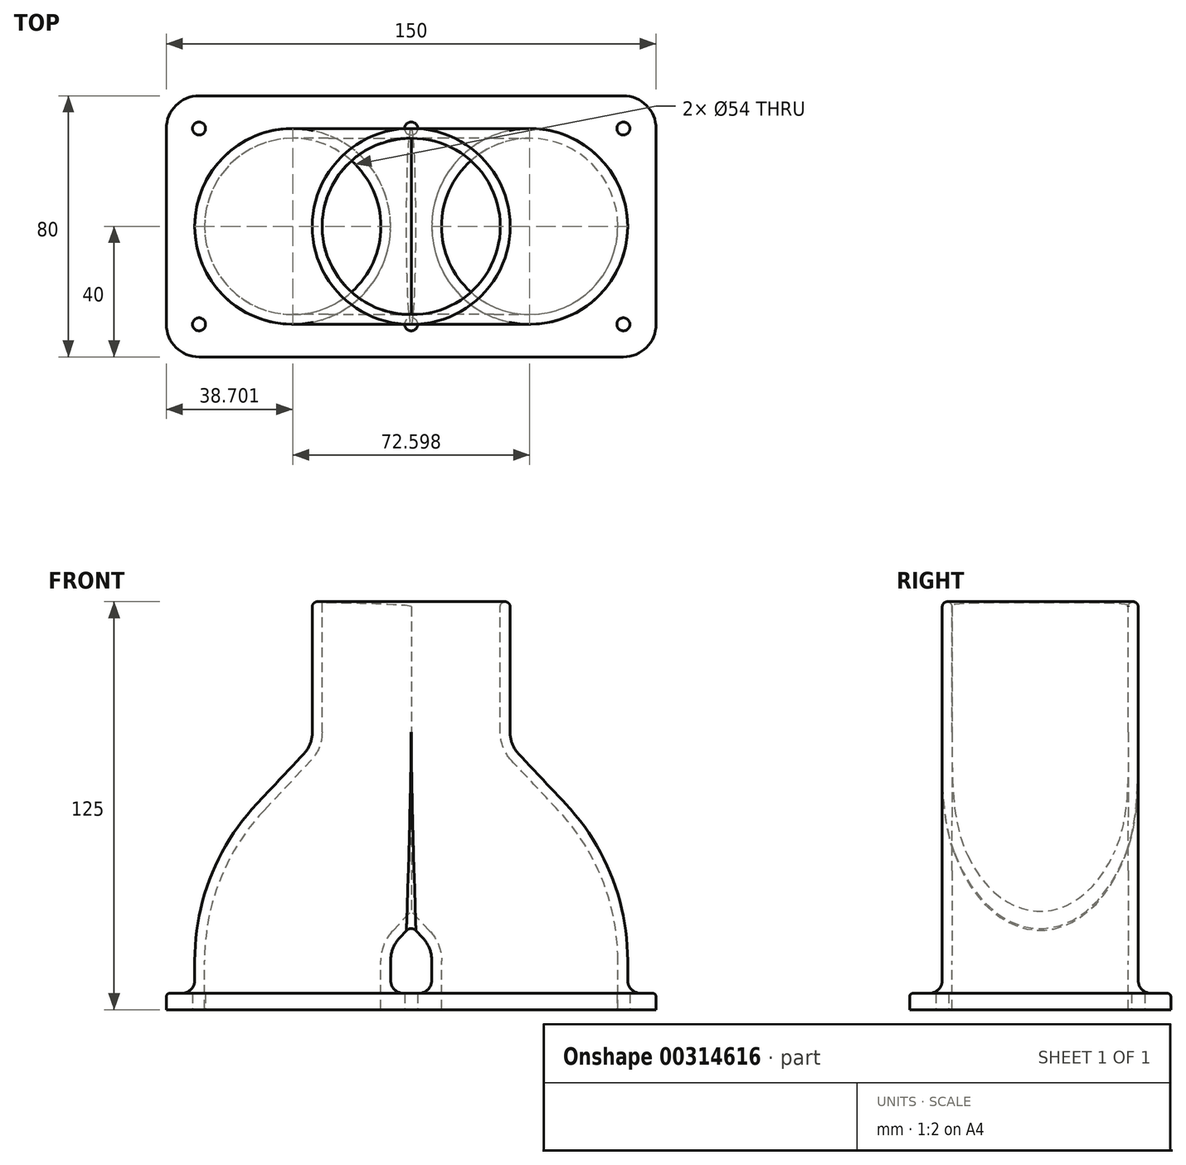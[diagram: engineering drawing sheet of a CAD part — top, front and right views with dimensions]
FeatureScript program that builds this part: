
annotation { "Feature Type Name" : "Feature", "Feature Type Description" : "" }
export const myFeature = defineFeature(function(context is Context, id is Id, definition is map)
    precondition{}
    {
        {
            var Q0;
            Q0=qCreatedBy(makeId("Front.planeOp"),FACE);
            var sketch = newSketch(context, id + "F0", { "sketchPlane" : qUnion([Q0])});
            skLineSegment(sketch, "E0", {"start": v(36, 0) * mm, "end": v(36, 15) * mm});
            skLineSegment(sketch, "E1", {"start": v(0, 125) * mm, "end": v(80.75, 125) * mm, "construction": true});
            skLineSegment(sketch, "E2", {"start": v(0, 85) * mm, "end": v(81.82, 85) * mm, "construction": true});
            skLineSegment(sketch, "E3", {"start": v(40, 109.76) * mm, "end": v(40, 63.63) * mm, "construction": true});
            skLineSegment(sketch, "E4", {"start": v(-4, 0) * mm, "end": v(-4, 33.23) * mm, "construction": true});
            skLineSegment(sketch, "E5", {"start": v(36, 15) * mm, "end": v(-30.05, 15) * mm, "construction": true});
            skArc(sketch, "E6", {"start": v(36, 15) * mm, "mid": v(33.19, 29.73) * mm, "end": v(25.15, 42.4) * mm});
            skArc(sketch, "E7", {"start": v(0, 85) * mm, "mid": v(2.81, 70.27) * mm, "end": v(10.85, 57.6) * mm});
            skLineSegment(sketch, "E8", {"start": v(25.15, 42.4) * mm, "end": v(10.85, 57.6) * mm});
            skLineSegment(sketch, "E9.trimOffspring", {"start": v(0, 85) * mm, "end": v(0, 125) * mm});
            skLineSegment(sketch, "E10", {"start": v(0, 0) * mm, "end": v(0, 134.4) * mm, "construction": true});
            skSolve(sketch);
        }
        {
            var Q0;
            Q0=qCreatedBy(makeId("Top.planeOp"),FACE);
            var sketch = newSketch(context, id + "F1", { "sketchPlane" : qUnion([Q0])});
            skCircle(sketch, "E11", {"center": v(36.3, 0) * mm, "radius": 30 * mm});
            skSolve(sketch);
        }
        {
            var Q0;
            Q0=makeQuery(id+"F1.imprint","IMPRINT",FACE,{"disambiguationData":[TD([[makeQuery(id+"F1.imprint","IMPRINT",EDGE,{"derivedFrom":sQuery(id+"F1.wireOp",EDGE,"E11")}),1.0]])]});
            var Q1;
            Q1=sQuery(id+"F0.wireOp",EDGE,"E0");
            var Q2;
            Q2=sQuery(id+"F0.wireOp",EDGE,"E6");
            var Q3;
            Q3=sQuery(id+"F0.wireOp",EDGE,"E8");
            var Q4;
            Q4=sQuery(id+"F0.wireOp",EDGE,"E7");
            var Q5;
            Q5=sQuery(id+"F0.wireOp",EDGE,"E9.trimOffspring");
            sweep(context, id + "F2", {"profiles" : qUnion([Q0]), "path" : qUnion([Q1, Q2, Q3, Q4, Q5])});
        }
        {
            var Q0;
            Q0=makeQuery(id+"F2.opSweep","SWEPT_BODY",BODY,{"disambiguationData":[OSD([sQuery(id+"F0.wireOp",EDGE,"E9.trimOffspring"),sQuery(id+"F1.wireOp",EDGE,"E11")])]});
            var Q1;
            Q1=qCreatedBy(makeId("Right.planeOp"),FACE);
            mirror(context, id + "F3", {"entities" : qUnion([Q0]), "mirrorPlane" : qUnion([Q1])});
        }
        {
            var Q0;
            Q0=makeQuery(id+"F3.opPattern","COPY",BODY,{"derivedFrom":makeQuery(id+"F2.opSweep","SWEPT_BODY",BODY,{"disambiguationData":[OSD([sQuery(id+"F0.wireOp",EDGE,"E9.trimOffspring"),sQuery(id+"F1.wireOp",EDGE,"E11")])]}),"instanceName":"1"});
            var Q1;
            Q1=makeQuery(id+"F2.opSweep","SWEPT_BODY",BODY,{"disambiguationData":[OSD([sQuery(id+"F0.wireOp",EDGE,"E9.trimOffspring"),sQuery(id+"F1.wireOp",EDGE,"E11")])]});
            booleanBodies(context, id + "F4", {"operationType" : BooleanOperationType.UNION, "tools" : qUnion([Q0, Q1])});
        }
        {
            var Q0;
            {var subQ0=makeQuery(id+"F2.opSweep","CAP_FACE",FACE,{"disambiguationData":[OSD([sQuery(id+"F0.wireOp",VERTEX,"E9.trimOffspring.end"),sQuery(id+"F1.wireOp",EDGE,"E11")])],"isStart":false});Q0=makeQuery(id+"F4.opBoolean","MERGE",FACE,{"derivedFrom":[subQ0,makeQuery(id+"F3.opPattern","COPY",FACE,{"derivedFrom":subQ0,"instanceName":"1"})]});}
            var Q1;
            Q1=makeQuery(id+"F2.opSweep","CAP_FACE",FACE,{"disambiguationData":[OSD([sQuery(id+"F0.wireOp",VERTEX,"E0.start"),sQuery(id+"F1.wireOp",EDGE,"E11")])],"isStart":true});
            var Q2;
            Q2=makeQuery(id+"F3.opPattern","COPY",FACE,{"derivedFrom":makeQuery(id+"F2.opSweep","CAP_FACE",FACE,{"disambiguationData":[OSD([sQuery(id+"F0.wireOp",VERTEX,"E0.start"),sQuery(id+"F1.wireOp",EDGE,"E11")])],"isStart":true}),"instanceName":"1"});
            shell(context, id + "F5", {"entities" : qUnion([Q0, Q1, Q2]), "thickness" : 3 * mm});
        }
        {
            var Q0;
            {var subQ0=makeQuery(id+"F2.opSweep","SWEPT_FACE",FACE,{"disambiguationData":[OSD([sQuery(id+"F0.wireOp",EDGE,"E8"),sQuery(id+"F1.wireOp",EDGE,"E11")])]});Q0=makeQuery(id+"F4.opBoolean","INTERSECT",EDGE,{"derivedFrom":[subQ0,makeQuery(id+"F3.opPattern","COPY",FACE,{"derivedFrom":subQ0,"instanceName":"1"})]});}
            fillet(context, id + "F6", {"entities" : qUnion([Q0]), "radius" : 2 * mm, "tangentPropagation" : true, "allowEdgeOverflow" : false});
        }
        {
            var Q0;
            Q0=qCreatedBy(makeId("Top.planeOp"),FACE);
            var sketch = newSketch(context, id + "F7", { "sketchPlane" : qUnion([Q0])});
            skLineSegment(sketch, "E12.bottom", {"start": v(-75, 40) * mm, "end": v(75, 40) * mm});
            skLineSegment(sketch, "E12.top", {"start": v(-75, -40) * mm, "end": v(75, -40) * mm});
            skLineSegment(sketch, "E12.left", {"start": v(-75, 40) * mm, "end": v(-75, -40) * mm});
            skLineSegment(sketch, "E12.right", {"start": v(75, 40) * mm, "end": v(75, -40) * mm});
            skPoint(sketch, "E13", {"position": v(-7.12, -183.95) * mm});
            skPoint(sketch, "E14", {"position": v(-65, -30) * mm});
            skPoint(sketch, "E15", {"position": v(65, -30) * mm});
            skPoint(sketch, "E16", {"position": v(65, 30) * mm});
            skPoint(sketch, "E17", {"position": v(-65, 30) * mm});
            skPoint(sketch, "E18", {"position": v(0, -30) * mm});
            skPoint(sketch, "E19", {"position": v(0, 30) * mm});
            skSolve(sketch);
        }
        {
            var Q0;
            Q0=makeQuery(id+"F7.imprint","IMPRINT",FACE,{"disambiguationData":[TD([[makeQuery(id+"F7.imprint","IMPRINT",EDGE,{"derivedFrom":sQuery(id+"F7.wireOp",EDGE,"E12.bottom")}),-1.0]])]});
            extrude(context, id + "F8", {"entities" : qUnion([Q0]), "operationType" : NewBodyOperationType.ADD, "depth" : 5 * mm});
        }
        {
            var Q0;
            {var subQ0=sQuery(id+"F1.wireOp",EDGE,"E11");var subQ1=sQuery(id+"F0.wireOp",EDGE,"E0");Q0=makeQuery(id+"F8.boolean.opBoolean","SPLIT",FACE,{"disambiguationData":[TD([makeQuery(id+"F5.opShell","OFFSET_FACE",FACE,{"disambiguationData":[OSD([subQ1,subQ0]),TDD([makeQuery(id+"F2.opSweep","SWEPT_FACE",FACE,{"disambiguationData":[OSD([subQ1,subQ0])]})])]})])],"derivedFrom":makeQuery(id+"F8.opExtrude","CAP_FACE",FACE,{"disambiguationData":[OSD([sQuery(id+"F7.wireOp",EDGE,"E12.bottom"),sQuery(id+"F7.wireOp",EDGE,"E12.top"),sQuery(id+"F7.wireOp",EDGE,"E12.left"),sQuery(id+"F7.wireOp",EDGE,"E12.right")])],"isStart":false})});}
            extrude(context, id + "F9", {"entities" : qUnion([Q0]), "operationType" : NewBodyOperationType.REMOVE, "oppositeDirection" : true, "depth" : 5 * mm});
        }
        {
            var Q0;
            {var subQ0=sQuery(id+"F1.wireOp",EDGE,"E11");var subQ1=sQuery(id+"F0.wireOp",EDGE,"E0");Q0=makeQuery(id+"F8.boolean.opBoolean","SPLIT",FACE,{"disambiguationData":[TD([makeQuery(id+"F5.opShell","OFFSET_FACE",FACE,{"disambiguationData":[OSD([subQ1,subQ0]),TDD([makeQuery(id+"F3.opPattern","COPY",FACE,{"derivedFrom":makeQuery(id+"F2.opSweep","SWEPT_FACE",FACE,{"disambiguationData":[OSD([subQ1,subQ0])]}),"instanceName":"1"})])]})])],"derivedFrom":makeQuery(id+"F8.opExtrude","CAP_FACE",FACE,{"disambiguationData":[OSD([sQuery(id+"F7.wireOp",EDGE,"E12.bottom"),sQuery(id+"F7.wireOp",EDGE,"E12.top"),sQuery(id+"F7.wireOp",EDGE,"E12.left"),sQuery(id+"F7.wireOp",EDGE,"E12.right")])],"isStart":false})});}
            extrude(context, id + "F10", {"entities" : qUnion([Q0]), "operationType" : NewBodyOperationType.REMOVE, "oppositeDirection" : true, "depth" : 5 * mm});
        }
        {
            var Q0;
            Q0=sQuery(id+"F7.wireOp",VERTEX,"E14");
            var Q1;
            Q1=sQuery(id+"F7.wireOp",VERTEX,"E15");
            var Q2;
            Q2=sQuery(id+"F7.wireOp",VERTEX,"E16");
            var Q3;
            Q3=sQuery(id+"F7.wireOp",VERTEX,"E17");
            var Q4;
            Q4=sQuery(id+"F7.wireOp",VERTEX,"E18");
            var Q5;
            Q5=sQuery(id+"F7.wireOp",VERTEX,"E19");
            var Q6;
            Q6=makeQuery(id+"F3.opPattern","COPY",BODY,{"derivedFrom":makeQuery(id+"F2.opSweep","SWEPT_BODY",BODY,{"disambiguationData":[OSD([sQuery(id+"F0.wireOp",EDGE,"E9.trimOffspring"),sQuery(id+"F1.wireOp",EDGE,"E11")])]}),"instanceName":"1"});
            hole(context, id + "F11", {"style" : HoleStyle.SIMPLE, "endStyle" : HoleEndStyle.BLIND, "oppositeDirection" : true, "holeDiameter" : 4 * mm, "holeDepth" : 5 * mm, "tappedDepth" : 12 * mm, "tapClearance" : 3, "startFromSketch" : true, "locations" : qUnion([Q0, Q1, Q2, Q3, Q4, Q5]), "scope" : qUnion([Q6])});
        }
        {
            var Q0;
            Q0=makeQuery(id+"F8.opExtrude","SWEPT_EDGE",EDGE,{"disambiguationData":[OSD([sQuery(id+"F7.wireOp",EDGE,"E12.top"),sQuery(id+"F7.wireOp",EDGE,"E12.right")])]});
            var Q1;
            Q1=makeQuery(id+"F8.opExtrude","SWEPT_EDGE",EDGE,{"disambiguationData":[OSD([sQuery(id+"F7.wireOp",EDGE,"E12.top"),sQuery(id+"F7.wireOp",EDGE,"E12.left")])]});
            var Q2;
            Q2=makeQuery(id+"F8.opExtrude","SWEPT_EDGE",EDGE,{"disambiguationData":[OSD([sQuery(id+"F7.wireOp",EDGE,"E12.bottom"),sQuery(id+"F7.wireOp",EDGE,"E12.right")])]});
            var Q3;
            Q3=makeQuery(id+"F8.opExtrude","SWEPT_EDGE",EDGE,{"disambiguationData":[OSD([sQuery(id+"F7.wireOp",EDGE,"E12.bottom"),sQuery(id+"F7.wireOp",EDGE,"E12.left")])]});
            fillet(context, id + "F12", {"entities" : qUnion([Q0, Q1, Q2, Q3]), "radius" : 10 * mm, "tangentPropagation" : true, "allowEdgeOverflow" : false});
        }
        {
            var Q0;
            {var subQ0=sQuery(id+"F7.wireOp",EDGE,"E12.top");var subQ2=sQuery(id+"F7.wireOp",EDGE,"E12.bottom");var subQ3=sQuery(id+"F7.wireOp",EDGE,"E12.left");var subQ4=sQuery(id+"F7.wireOp",EDGE,"E12.right");Q0=makeQuery(id+"F12.opFillet","BLEND_EDGE",EDGE,{"blendedFrom":[makeQuery(id+"F8.opExtrude","SWEPT_EDGE",EDGE,{"disambiguationData":[OSD([subQ0,subQ3])]}),makeQuery(id+"F8.boolean.opBoolean","SPLIT",FACE,{"disambiguationData":[TD([makeQuery(id+"F8.opExtrude","SWEPT_FACE",FACE,{"disambiguationData":[OSD([subQ2])]})])],"derivedFrom":makeQuery(id+"F8.opExtrude","CAP_FACE",FACE,{"disambiguationData":[OSD([subQ2,subQ0,subQ3,subQ4])],"isStart":false})})],"blendedInto":[makeQuery(id+"F8.boolean.opBoolean","SPLIT",FACE,{"disambiguationData":[TD([makeQuery(id+"F8.opExtrude","SWEPT_FACE",FACE,{"disambiguationData":[OSD([subQ2])]})])],"derivedFrom":makeQuery(id+"F8.opExtrude","CAP_FACE",FACE,{"disambiguationData":[OSD([subQ2,subQ0,subQ3,subQ4])],"isStart":false})})]});}
            var Q1;
            Q1=makeQuery(id+"F8.opExtrude","CAP_EDGE",EDGE,{"disambiguationData":[OSD([sQuery(id+"F7.wireOp",EDGE,"E12.left")])],"isStart":false});
            var Q2;
            Q2=makeQuery(id+"F8.opExtrude","CAP_EDGE",EDGE,{"disambiguationData":[OSD([sQuery(id+"F7.wireOp",EDGE,"E12.top")])],"isStart":false});
            var Q3;
            {var subQ0=sQuery(id+"F7.wireOp",EDGE,"E12.top");var subQ2=sQuery(id+"F7.wireOp",EDGE,"E12.bottom");var subQ3=sQuery(id+"F7.wireOp",EDGE,"E12.left");var subQ4=sQuery(id+"F7.wireOp",EDGE,"E12.right");Q3=makeQuery(id+"F12.opFillet","BLEND_EDGE",EDGE,{"blendedFrom":[makeQuery(id+"F8.opExtrude","SWEPT_EDGE",EDGE,{"disambiguationData":[OSD([subQ0,subQ4])]}),makeQuery(id+"F8.boolean.opBoolean","SPLIT",FACE,{"disambiguationData":[TD([makeQuery(id+"F8.opExtrude","SWEPT_FACE",FACE,{"disambiguationData":[OSD([subQ2])]})])],"derivedFrom":makeQuery(id+"F8.opExtrude","CAP_FACE",FACE,{"disambiguationData":[OSD([subQ2,subQ0,subQ3,subQ4])],"isStart":false})})],"blendedInto":[makeQuery(id+"F8.boolean.opBoolean","SPLIT",FACE,{"disambiguationData":[TD([makeQuery(id+"F8.opExtrude","SWEPT_FACE",FACE,{"disambiguationData":[OSD([subQ2])]})])],"derivedFrom":makeQuery(id+"F8.opExtrude","CAP_FACE",FACE,{"disambiguationData":[OSD([subQ2,subQ0,subQ3,subQ4])],"isStart":false})})]});}
            fillet(context, id + "F13", {"entities" : qUnion([Q0, Q1, Q2, Q3]), "radius" : 1 * mm, "tangentPropagation" : true, "allowEdgeOverflow" : false});
        }
        {
            var Q0;
            Q0=makeQuery(id+"F8.boolean.opBoolean","INTERSECT",EDGE,{"derivedFrom":[makeQuery(id+"F3.opPattern","COPY",FACE,{"derivedFrom":makeQuery(id+"F2.opSweep","SWEPT_FACE",FACE,{"disambiguationData":[OSD([sQuery(id+"F0.wireOp",EDGE,"E0"),sQuery(id+"F1.wireOp",EDGE,"E11")])]}),"instanceName":"1"}),makeQuery(id+"F8.opExtrude","CAP_FACE",FACE,{"disambiguationData":[OSD([sQuery(id+"F7.wireOp",EDGE,"E12.bottom"),sQuery(id+"F7.wireOp",EDGE,"E12.top"),sQuery(id+"F7.wireOp",EDGE,"E12.left"),sQuery(id+"F7.wireOp",EDGE,"E12.right")])],"isStart":false})]});
            var Q1;
            Q1=makeQuery(id+"F8.boolean.opBoolean","INTERSECT",EDGE,{"derivedFrom":[makeQuery(id+"F2.opSweep","SWEPT_FACE",FACE,{"disambiguationData":[OSD([sQuery(id+"F0.wireOp",EDGE,"E0"),sQuery(id+"F1.wireOp",EDGE,"E11")])]}),makeQuery(id+"F8.opExtrude","CAP_FACE",FACE,{"disambiguationData":[OSD([sQuery(id+"F7.wireOp",EDGE,"E12.bottom"),sQuery(id+"F7.wireOp",EDGE,"E12.top"),sQuery(id+"F7.wireOp",EDGE,"E12.left"),sQuery(id+"F7.wireOp",EDGE,"E12.right")])],"isStart":false})]});
            fillet(context, id + "F14", {"entities" : qUnion([Q0, Q1]), "radius" : 4 * mm, "tangentPropagation" : true, "allowEdgeOverflow" : false});
        }
        {
            var Q0;
            Q0=makeQuery(id+"F2.opSweep","CAP_EDGE",EDGE,{"disambiguationData":[OSD([sQuery(id+"F0.wireOp",VERTEX,"E9.trimOffspring.end"),sQuery(id+"F1.wireOp",EDGE,"E11")])],"isStart":false});
            var Q1;
            {var subQ0=sQuery(id+"F1.wireOp",EDGE,"E11");var subQ1=sQuery(id+"F0.wireOp",VERTEX,"E9.trimOffspring.end");Q1=makeQuery(id+"F5.opShell","OFFSET_EDGE",EDGE,{"disambiguationData":[OSD([subQ1,subQ0]),TDD([makeQuery(id+"F2.opSweep","CAP_EDGE",EDGE,{"disambiguationData":[OSD([subQ1,subQ0])],"isStart":false})])]});}
            fillet(context, id + "F15", {"entities" : qUnion([Q0, Q1]), "radius" : 1.5 * mm, "tangentPropagation" : true, "allowEdgeOverflow" : false});
        }
    });
